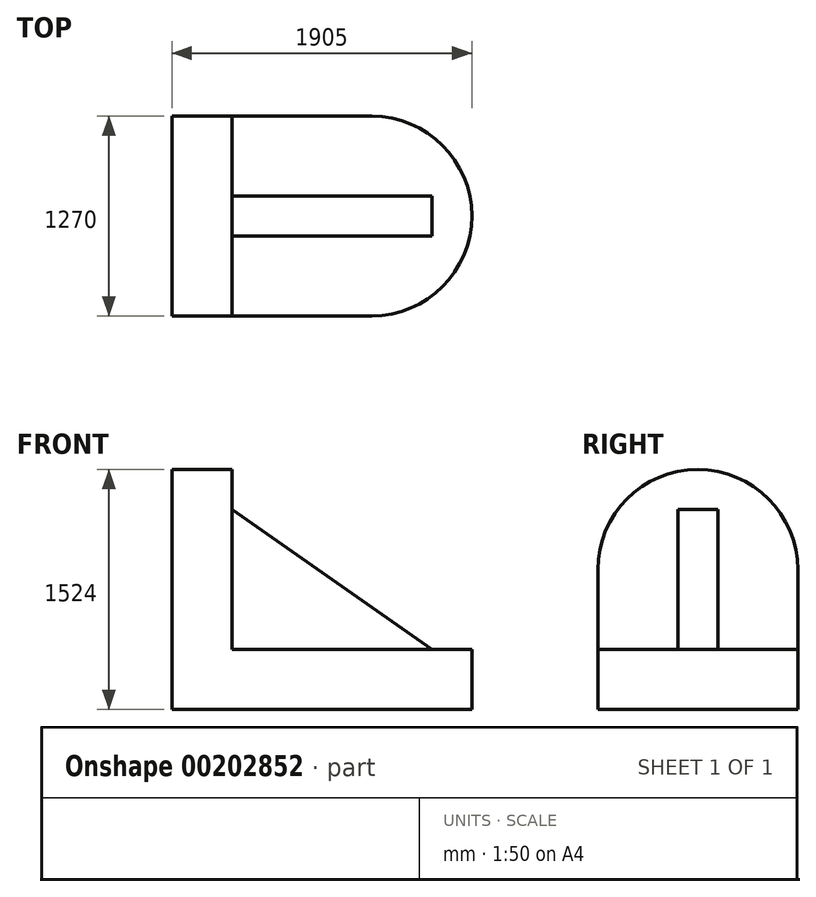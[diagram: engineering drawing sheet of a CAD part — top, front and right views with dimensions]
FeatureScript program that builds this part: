
annotation { "Feature Type Name" : "Feature", "Feature Type Description" : "" }
export const myFeature = defineFeature(function(context is Context, id is Id, definition is map)
    precondition{}
    {
        {
            var Q0;
            Q0=qCreatedBy(makeId("Front.planeOp"),FACE);
            var sketch = newSketch(context, id + "F0", { "sketchPlane" : qUnion([Q0])});
            skLineSegment(sketch, "E0.bottom", {"start": v(0, 0) * mm, "end": v(1270, 0) * mm});
            skLineSegment(sketch, "E0.top", {"start": v(0, 889) * mm, "end": v(381, 889) * mm});
            skLineSegment(sketch, "E0.left", {"start": v(0, 0) * mm, "end": v(0, 889) * mm});
            skLineSegment(sketch, "E0.right", {"start": v(1270, 0) * mm, "end": v(1270, 381) * mm});
            skLineSegment(sketch, "E1.top", {"start": v(381, 381) * mm, "end": v(1270, 381) * mm});
            skLineSegment(sketch, "E1.left", {"start": v(381, 889) * mm, "end": v(381, 381) * mm});
            skSolve(sketch);
        }
        {
            var Q0;
            Q0 = qSketchRegion(id + "F0", true);
            extrude(context, id + "F1", {"entities" : qUnion([Q0]), "depth" : 1270 * mm});
        }
        {
            var Q0;
            Q0=makeQuery(id+"F1.opExtrude","SWEPT_FACE",FACE,{"disambiguationData":[OSD([sQuery(id+"F0.wireOp",EDGE,"E1.left")])]});
            var sketch = newSketch(context, id + "F2", { "sketchPlane" : qUnion([Q0])});
            skArc(sketch, "E2", {"start": v(0, 889) * mm, "mid": v(-635, 1524) * mm, "end": v(-1270, 889) * mm});
            skLineSegment(sketch, "E3", {"start": v(-1270, 889) * mm, "end": v(0, 889) * mm});
            skLineSegment(sketch, "E4", {"start": v(-1270, 889) * mm, "end": v(-1270, 1617.57) * mm, "construction": true});
            skLineSegment(sketch, "E5", {"start": v(-1270, 1617.57) * mm, "end": v(0, 1442.45) * mm, "construction": true});
            skLineSegment(sketch, "E6", {"start": v(0, 1442.45) * mm, "end": v(0, 889) * mm, "construction": true});
            skSolve(sketch);
        }
        {
            var Q0;
            Q0 = qSketchRegion(id + "F2", true);
            var Q1;
            Q1=makeQuery(id+"F1.opExtrude","SWEPT_FACE",FACE,{"disambiguationData":[OSD([sQuery(id+"F0.wireOp",EDGE,"E0.left")])]});
            extrude(context, id + "F3", {"entities" : qUnion([Q0]), "operationType" : NewBodyOperationType.ADD, "endBound" : BoundingType.UP_TO_SURFACE, "oppositeDirection" : true, "endBoundEntityFace" : qUnion([Q1]), "depth" : 525.78 * mm});
        }
        {
            var Q0;
            Q0=makeQuery(id+"F1.opExtrude","SWEPT_FACE",FACE,{"disambiguationData":[OSD([sQuery(id+"F0.wireOp",EDGE,"E1.top")])]});
            var sketch = newSketch(context, id + "F4", { "sketchPlane" : qUnion([Q0])});
            skArc(sketch, "E7", {"start": v(1270, -1270) * mm, "mid": v(1905, -635) * mm, "end": v(1270, 0) * mm});
            skLineSegment(sketch, "E8", {"start": v(1270, -1270) * mm, "end": v(1270, 0) * mm, "construction": true});
            skLineSegment(sketch, "E9", {"start": v(1270, 0) * mm, "end": v(1905, 0) * mm, "construction": true});
            skPoint(sketch, "E9.endSnap0", {"position": v(1905, -635) * mm});
            skLineSegment(sketch, "E10", {"start": v(1905, 0) * mm, "end": v(1905, -1270) * mm, "construction": true});
            skLineSegment(sketch, "E11", {"start": v(1905, -1270) * mm, "end": v(1270, -1270) * mm, "construction": true});
            skSolve(sketch);
        }
        {
            var Q0;
            Q0 = qSketchRegion(id + "F4", true);
            var Q1;
            Q1=makeQuery(id+"F4.imprint","IMPRINT",FACE,{"disambiguationData":[TD([[makeQuery(id+"F4.imprint","IMPRINT",EDGE,{"derivedFrom":sQuery(id+"F4.wireOp",EDGE,"E7")}),1.0]])]});
            var Q2;
            Q2=makeQuery(id+"F1.opExtrude","SWEPT_FACE",FACE,{"disambiguationData":[OSD([sQuery(id+"F0.wireOp",EDGE,"E0.bottom")])]});
            extrude(context, id + "F5", {"entities" : qUnion([Q0, Q1]), "operationType" : NewBodyOperationType.ADD, "endBound" : BoundingType.UP_TO_SURFACE, "oppositeDirection" : true, "endBoundEntityFace" : qUnion([Q2]), "depth" : 690.88 * mm});
        }
        {
            var Q0;
            Q0=makeQuery(id+"F1.opExtrude","CAP_FACE",FACE,{"disambiguationData":[OSD([sQuery(id+"F0.wireOp",EDGE,"E0.bottom"),sQuery(id+"F0.wireOp",EDGE,"E0.top"),sQuery(id+"F0.wireOp",EDGE,"E0.left"),sQuery(id+"F0.wireOp",EDGE,"E0.right"),sQuery(id+"F0.wireOp",EDGE,"E1.top"),sQuery(id+"F0.wireOp",EDGE,"E1.left")])],"isStart":false});
            var sketch = newSketch(context, id + "F6", { "sketchPlane" : qUnion([Q0])});
            skLineSegment(sketch, "E12", {"start": v(381, 1270) * mm, "end": v(1651, 381) * mm});
            skLineSegment(sketch, "E13", {"start": v(381, 1270) * mm, "end": v(381, 381) * mm});
            skLineSegment(sketch, "E14", {"start": v(381, 381) * mm, "end": v(1651, 381) * mm});
            skSolve(sketch);
        }
        {
            var Q0;
            Q0=makeQuery(id+"F6.imprint","IMPRINT",FACE,{"disambiguationData":[TD([[makeQuery(id+"F6.imprint","IMPRINT",EDGE,{"derivedFrom":sQuery(id+"F6.wireOp",EDGE,"ssf8Botf-163t-IXrB-ch0B-oopAp7STTjui")}),-1.0]])]});
            var Q1;
            {var subQ7=sQuery(id+"F6.wireOp",EDGE,"E12");Q1=makeQuery(id+"F6.imprint","IMPRINT",FACE,{"disambiguationData":[TD([[makeQuery(id+"F6.imprint","IMPRINT",EDGE,{"derivedFrom":subQ7}),-1.0]])]});}
            extrude(context, id + "F7", {"entities" : qUnion([Q0, Q1]), "oppositeDirection" : true, "depth" : 762 * mm, "hasSecondDirection" : true, "secondDirectionOppositeDirection" : true, "secondDirectionDepth" : 508 * mm});
        }
    });
